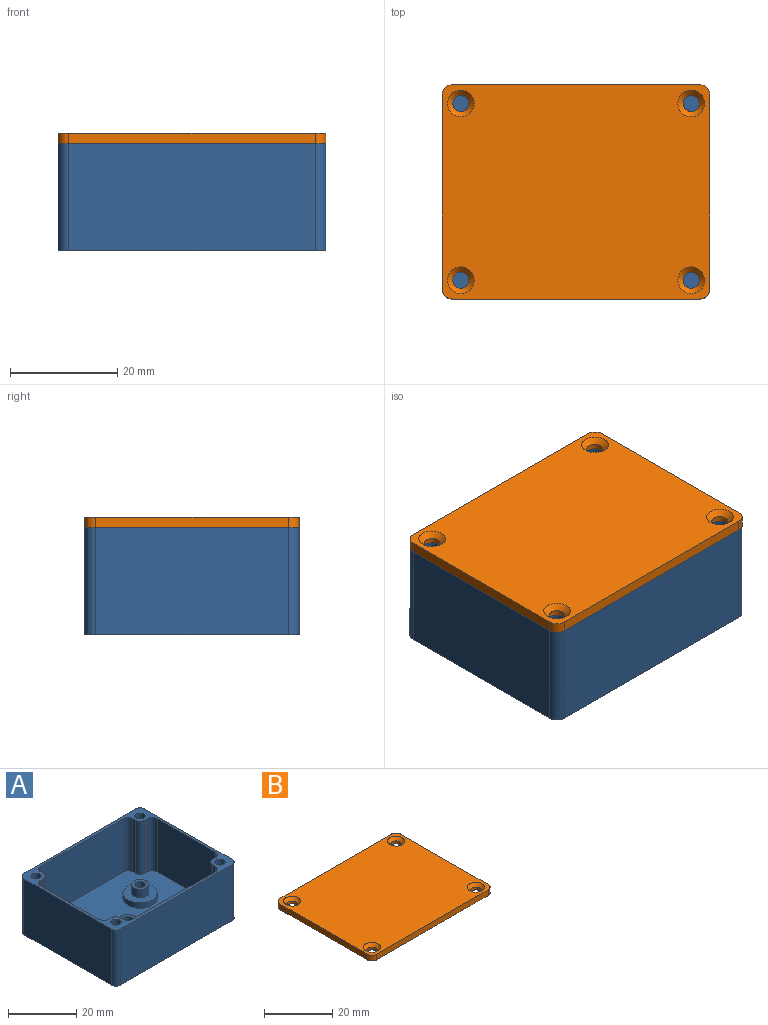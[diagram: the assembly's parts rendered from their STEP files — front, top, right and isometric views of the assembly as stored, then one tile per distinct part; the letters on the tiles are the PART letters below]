
ASSEMBLY  parts=2 mates=1
PART A: 67 faces, bbox 50x40x20 mm
  f0: plane 50x40mm, normal (0,0,-1), area 1949.8mm2, adj f9,f10,f11,f12,f37,f38,f39,f40
  f1: cylinder r=1.5mm len=4mm, axis (0,0,-1), area 37.7mm2, adj f30,f50
  f2: cylinder r=1.5mm len=4mm, axis (0,0,-1), area 37.7mm2, adj f32,f43
  f3: plane 48x38mm, normal (0,0,1), area 1563.5mm2, adj f4,f5,f6,f7,f13,f14,f15,f16
  f4: plane 34x19mm, normal (0,1,0), area 646mm2, adj f3,f8,f56,f58
  f5: plane 24x19mm, normal (-1,0,0), area 456mm2, adj f3,f8,f60,f61
  f6: plane 34x19mm, normal (0,-1,0), area 646mm2, adj f3,f8,f62,f64
  f7: plane 24x19mm, normal (1,0,0), area 456mm2, adj f3,f8,f57,f66
  f8: plane 50x40mm, normal (0,0,1), area 247.7mm2, adj f4,f5,f6,f7,f9,f10,f11,f12
  f9: plane 46x20mm, normal (0,1,0), area 920mm2, adj f0,f8,f51,f54
  f10: plane 36x20mm, normal (-1,0,0), area 720mm2, adj f0,f8,f51,f52
  f11: plane 46x20mm, normal (0,-1,0), area 920mm2, adj f0,f8,f52,f53
  f12: plane 36x20mm, normal (1,0,0), area 720mm2, adj f0,f8,f53,f54
  f13: plane 19x1mm, normal (0,-1,0), area 19mm2, adj f3,f8,f65,f66
  f14: plane 19x1mm, normal (1,0,0), area 19mm2, adj f3,f8,f64,f65
  f15: plane 19x1mm, normal (0,-1,0), area 19mm2, adj f3,f8,f61,f63
  f16: plane 19x1mm, normal (-1,0,0), area 19mm2, adj f3,f8,f62,f63
  f17: plane 19x1mm, normal (0,1,0), area 19mm2, adj f3,f8,f55,f57
  f18: plane 19x1mm, normal (1,0,0), area 19mm2, adj f3,f8,f55,f56
  f19: plane 19x1mm, normal (0,1,0), area 19mm2, adj f3,f8,f59,f60
  f20: plane 19x1mm, normal (-1,0,0), area 19mm2, adj f3,f8,f58,f59
  f21: cylinder r=1.5mm len=10mm, axis (0,0,1), area 94.2mm2, adj f8,f22
  f22: plane 3x3mm, normal (0,0,1), area 7.1mm2, adj f21
  f23: cylinder r=1.5mm len=10mm, axis (0,0,1), area 94.2mm2, adj f8,f24
  f24: plane 3x3mm, normal (0,0,1), area 7.1mm2, adj f23
  f25: cylinder r=1.5mm len=10mm, axis (0,0,1), area 94.2mm2, adj f8,f26
  f26: plane 3x3mm, normal (0,0,1), area 7.1mm2, adj f25
  f27: cylinder r=1.5mm len=10mm, axis (0,0,1), area 94.2mm2, adj f8,f28
  f28: plane 3x3mm, normal (0,0,1), area 7.1mm2, adj f27
  f29: cylinder r=2.5mm len=5mm, axis (0,0,-1), area 47.1mm2, adj f30,f34
  f30: plane 5x5mm, normal (0,0,1), area 12.6mm2, adj f1,f29
  f31: cylinder r=2.5mm len=5mm, axis (0,0,-1), area 47.1mm2, adj f32,f36
  f32: plane 5x5mm, normal (0,0,1), area 12.6mm2, adj f2,f31
  f33: cylinder r=5mm len=10mm, axis (0,0,-1), area 62.8mm2, adj f3,f34
  f34: plane 10x10mm, normal (0,0,1), area 58.9mm2, adj f29,f33
  f35: cylinder r=5mm len=10mm, axis (0,0,-1), area 62.8mm2, adj f3,f36
  f36: plane 10x10mm, normal (0,0,1), area 58.9mm2, adj f31,f35
  f37: plane 2.99x2mm, normal (0.07,-1,0), area 6mm2, adj f0,f38,f42,f43
  f38: plane 2.48x2mm, normal (-0.83,-0.56,0), area 6mm2, adj f0,f37,f39,f43
  f39: plane 2.7x2mm, normal (-0.9,0.44,0), area 6mm2, adj f0,f38,f40,f43
  f40: plane 2.99x2mm, normal (-0.07,1,0), area 6mm2, adj f0,f39,f41,f43
  f41: plane 2.48x2mm, normal (0.83,0.56,0), area 6mm2, adj f0,f40,f42,f43
  f42: plane 2.7x2mm, normal (0.9,-0.44,0), area 6mm2, adj f0,f37,f41,f43
  f43: plane 5.98x5.4mm, normal (0,0,-1), area 16.3mm2, adj f2,f37,f38,f39,f40,f41,f42
  f44: plane 2.96x2mm, normal (0.15,-0.99,0), area 6mm2, adj f0,f45,f49,f50
  f45: plane 2.34x2mm, normal (-0.78,-0.63,0), area 6mm2, adj f0,f44,f46,f50
  f46: plane 2.8x2mm, normal (-0.93,0.36,0), area 6mm2, adj f0,f45,f47,f50
  f47: plane 2.96x2mm, normal (-0.15,0.99,0), area 6mm2, adj f0,f46,f48,f50
  f48: plane 2.34x2mm, normal (0.78,0.63,0), area 6mm2, adj f0,f47,f49,f50
  f49: plane 2.8x2mm, normal (0.93,-0.36,0), area 6mm2, adj f0,f44,f48,f50
  f50: plane 5.93x5.59mm, normal (0,0,-1), area 16.3mm2, adj f1,f44,f45,f46,f47,f48,f49
  f51: cylinder r=2mm len=20mm, axis (0,0,1), area 62.8mm2, adj f0,f8,f9,f10
  f52: cylinder r=2mm len=20mm, axis (0,0,-1), area 62.8mm2, adj f0,f8,f10,f11
  f53: cylinder r=2mm len=20mm, axis (0,0,1), area 62.8mm2, adj f0,f8,f11,f12
  f54: cylinder r=2mm len=20mm, axis (0,0,-1), area 62.8mm2, adj f0,f8,f9,f12
  f55: cylinder r=2mm len=19mm, axis (0,0,1), area 59.7mm2, adj f3,f8,f17,f18
  f56: cylinder r=2mm len=19mm, axis (0,0,1), area 59.7mm2, adj f3,f4,f8,f18
  f57: cylinder r=2mm len=19mm, axis (0,0,-1), area 59.7mm2, adj f3,f7,f8,f17
  f58: cylinder r=2mm len=19mm, axis (0,0,-1), area 59.7mm2, adj f3,f4,f8,f20
  f59: cylinder r=2mm len=19mm, axis (0,0,1), area 59.7mm2, adj f3,f8,f19,f20
  f60: cylinder r=2mm len=19mm, axis (0,0,-1), area 59.7mm2, adj f3,f5,f8,f19
  f61: cylinder r=2mm len=19mm, axis (0,0,1), area 59.7mm2, adj f3,f5,f8,f15
  f62: cylinder r=2mm len=19mm, axis (0,0,-1), area 59.7mm2, adj f3,f6,f8,f16
  f63: cylinder r=2mm len=19mm, axis (0,0,1), area 59.7mm2, adj f3,f8,f15,f16
  f64: cylinder r=2mm len=19mm, axis (0,0,1), area 59.7mm2, adj f3,f6,f8,f14
  f65: cylinder r=2mm len=19mm, axis (0,0,1), area 59.7mm2, adj f3,f8,f13,f14
  f66: cylinder r=2mm len=19mm, axis (0,0,1), area 59.7mm2, adj f3,f7,f8,f13
PART B: 18 faces, bbox 50x40x2 mm
  f0: plane 46x2mm, normal (0,1,0), area 92mm2, adj f4,f5,f14,f17
  f1: plane 36x2mm, normal (-1,0,0), area 72mm2, adj f4,f5,f14,f15
  f2: plane 46x2mm, normal (0,-1,0), area 92mm2, adj f4,f5,f15,f16
  f3: plane 36x2mm, normal (1,0,0), area 72mm2, adj f4,f5,f16,f17
  f4: plane 50x40mm, normal (0,0,1), area 1918mm2, adj f0,f1,f2,f3,f10,f11,f12,f13
  f5: plane 50x40mm, normal (0,0,-1), area 1968.3mm2, adj f0,f1,f2,f3,f6,f7,f8,f9
  f6: cylinder r=1.5mm len=3mm, axis (0,0,1), area 9.4mm2, adj f5,f11
  f7: cylinder r=1.5mm len=3mm, axis (0,0,1), area 9.4mm2, adj f5,f13
  f8: cylinder r=1.5mm len=3mm, axis (0,0,1), area 9.4mm2, adj f5,f12
  f9: cylinder r=1.5mm len=3mm, axis (0,0,1), area 9.4mm2, adj f5,f10
  f10: cone r=1.5mm half-angle=45deg, axis (0,0,1), area 17.8mm2, adj f4,f9
  f11: cone r=1.5mm half-angle=45deg, axis (0,0,1), area 17.8mm2, adj f4,f6
  f12: cone r=1.5mm half-angle=45deg, axis (0,0,1), area 17.8mm2, adj f4,f8
  f13: cone r=1.5mm half-angle=45deg, axis (0,0,1), area 17.8mm2, adj f4,f7
  f14: cylinder r=2mm len=2mm, axis (0,0,1), area 6.3mm2, adj f0,f1,f4,f5
  f15: cylinder r=2mm len=2mm, axis (0,0,-1), area 6.3mm2, adj f1,f2,f4,f5
  f16: cylinder r=2mm len=2mm, axis (0,0,1), area 6.3mm2, adj f2,f3,f4,f5
  f17: cylinder r=2mm len=2mm, axis (0,0,-1), area 6.3mm2, adj f0,f3,f4,f5
PLACE A t=(-32.5,-16.95,18.72)mm fixed
PLACE B t=(-102.75,-20.97,38.72)mm
MATE slider A.f25 <-> B.f6  axis (0,0,1) through (-88.31,4.56,38.72)mm
